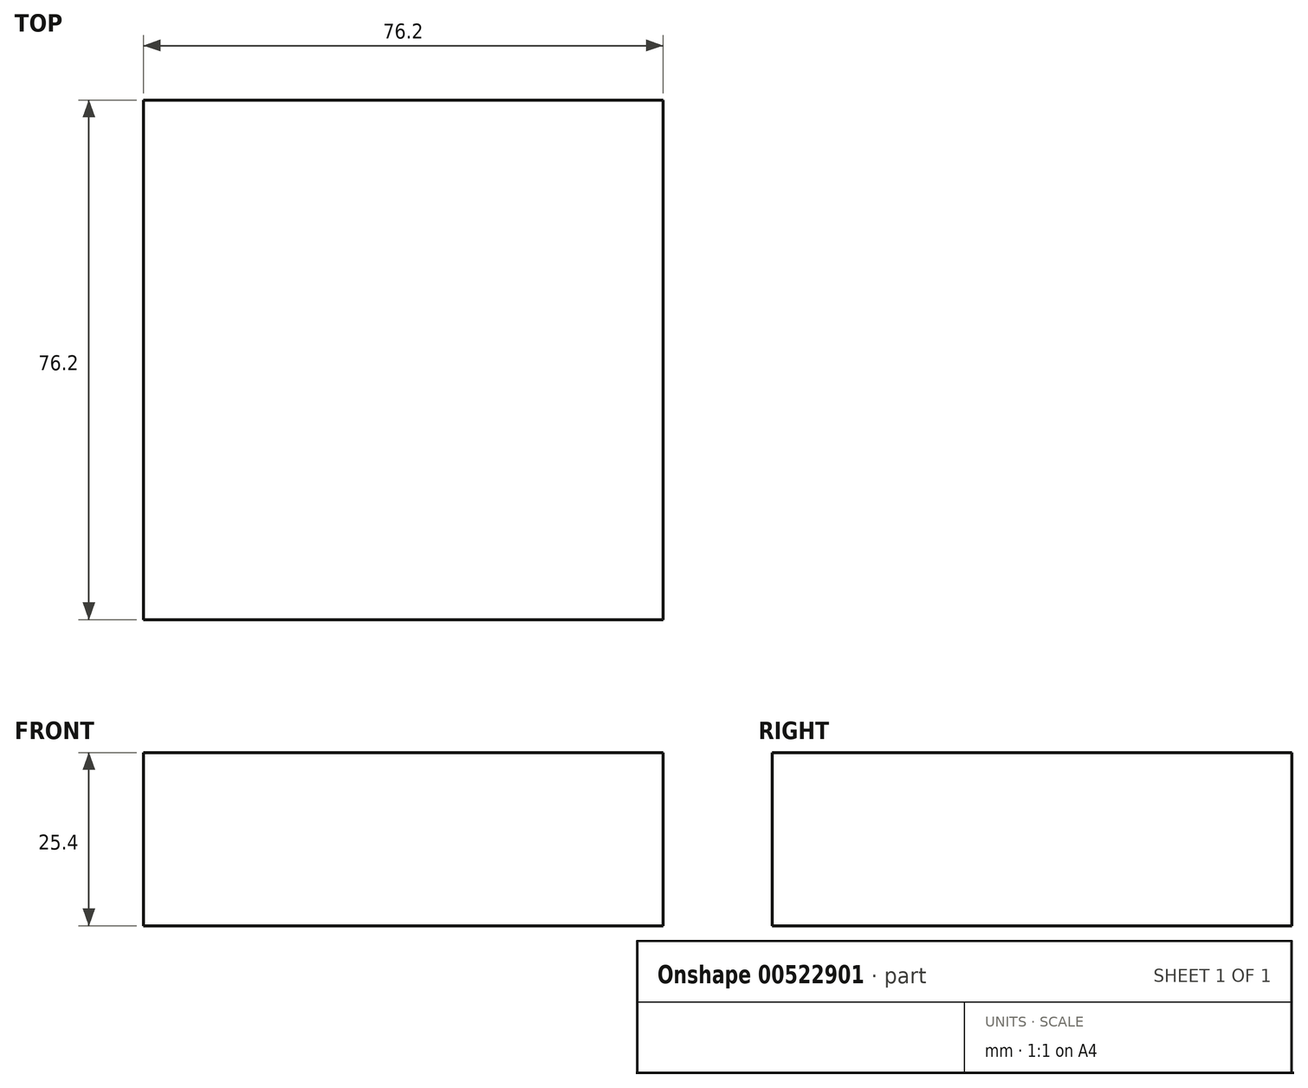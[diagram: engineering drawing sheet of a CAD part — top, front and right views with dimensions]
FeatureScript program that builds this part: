
annotation { "Feature Type Name" : "Feature", "Feature Type Description" : "" }
export const myFeature = defineFeature(function(context is Context, id is Id, definition is map)
    precondition{}
    {
        {
            var Q0;
            Q0=qCreatedBy(makeId("Top.planeOp"),FACE);
            var sketch = newSketch(context, id + "F0", { "sketchPlane" : qUnion([Q0])});
            skLineSegment(sketch, "E0.bottom", {"start": v(38.1, -38.1) * mm, "end": v(-38.1, -38.1) * mm});
            skLineSegment(sketch, "E0.top", {"start": v(38.1, 38.1) * mm, "end": v(-38.1, 38.1) * mm});
            skLineSegment(sketch, "E0.left", {"start": v(38.1, -38.1) * mm, "end": v(38.1, 38.1) * mm});
            skLineSegment(sketch, "E0.right", {"start": v(-38.1, -38.1) * mm, "end": v(-38.1, 38.1) * mm});
            skPoint(sketch, "E0.middle", {"position": v(0, 0) * mm});
            skSolve(sketch);
        }
        {
            var Q0;
            Q0=makeQuery(id+"F0.imprint","IMPRINT",FACE,{"disambiguationData":[TD([[makeQuery(id+"F0.imprint","IMPRINT",EDGE,{"derivedFrom":sQuery(id+"F0.wireOp",EDGE,"E0.bottom")}),-1.0]])]});
            extrude(context, id + "F1", {"entities" : qUnion([Q0]), "depth" : 25.4 * mm, "offsetDistance" : 25.4 * mm});
        }
    });
